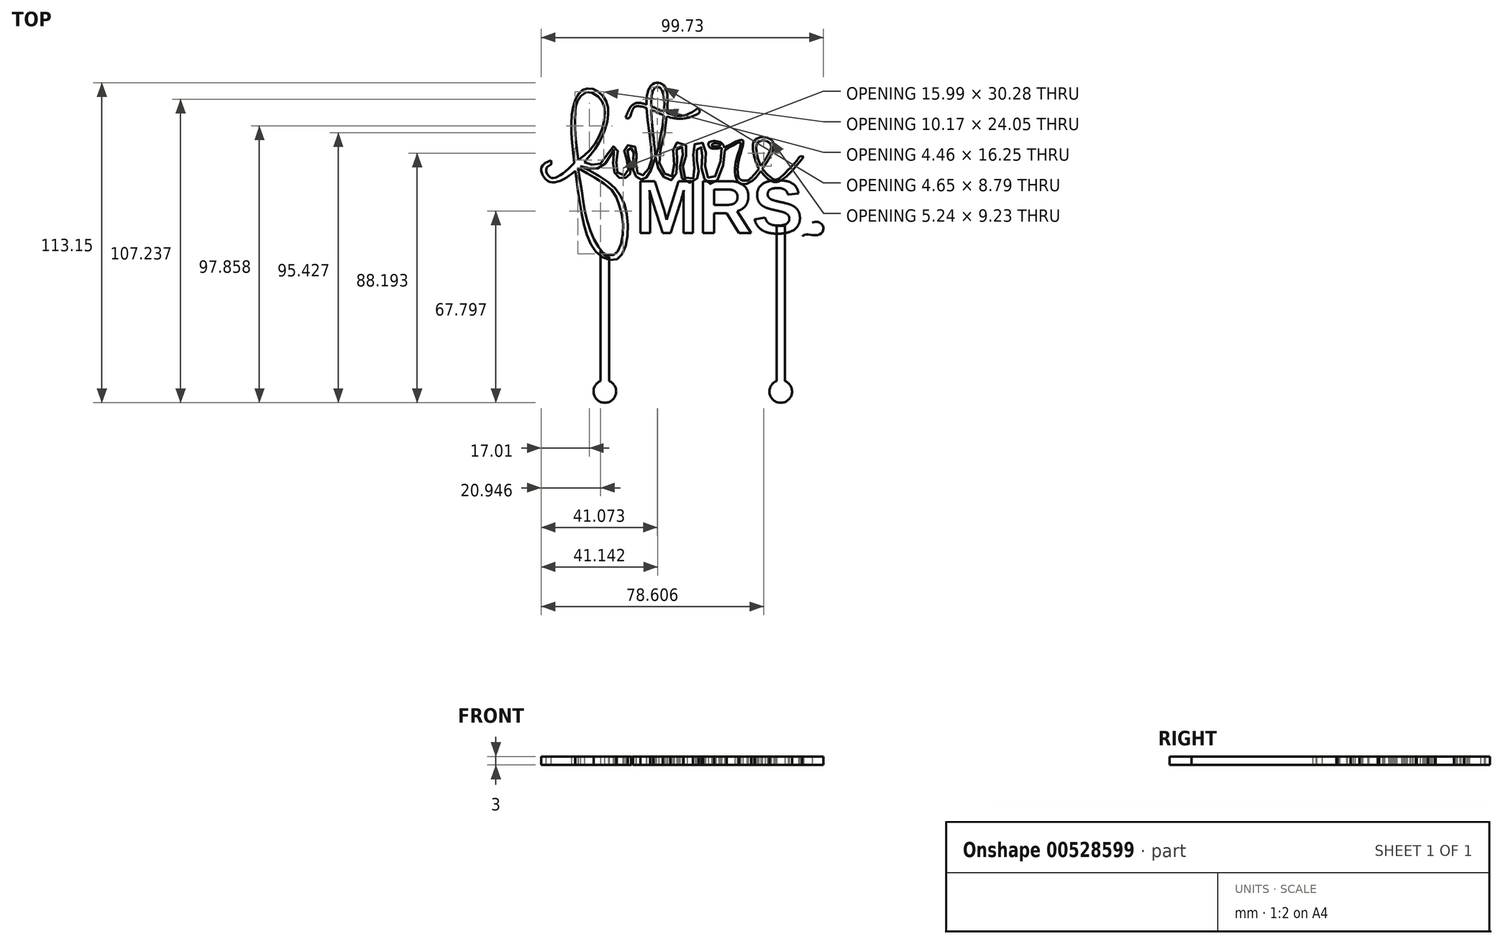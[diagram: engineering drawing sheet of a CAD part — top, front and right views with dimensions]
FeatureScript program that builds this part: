
annotation { "Feature Type Name" : "Feature", "Feature Type Description" : "" }
export const myFeature = defineFeature(function(context is Context, id is Id, definition is map)
    precondition{}
    {
        {
            var Q0;
            Q0=qCreatedBy(makeId("Top.planeOp"),FACE);
            var sketch = newSketch(context, id + "F0", { "sketchPlane" : qUnion([Q0])});
            skFitSpline(sketch, "E0", {"points": [v(-51.87, 23.02) * mm, v(-55.24, 20.26) * mm, v(-52.02, 15.35) * mm, v(-40.05, 22.4) * mm, v(-32.53, 34.53) * mm, v(-32.84, 44.96) * mm, v(-39.6, 48.34) * mm, v(-44.2, 40.97) * mm, v(-43.27, 19.8) * mm], "startDerivative": vector(-56.95, -24.54) * mm, "endDerivative": vector(16.5, -127.47) * mm});
            skFitSpline(sketch, "E1", {"points": [v(-43.27, 19.8) * mm, v(-40.66, 2.76) * mm, v(-35.45, -9.82) * mm, v(-28.08, -11.66) * mm, v(-24.7, 0) * mm, v(-28.85, 12.74) * mm, v(-41.42, 21.01) * mm], "startDerivative": vector(11.66, -89.63) * mm, "endDerivative": vector(-80.17, 39.6) * mm});
            skFitSpline(sketch, "E2", {"points": [v(-41.42, 21.01) * mm, v(-33.59, 21.01) * mm, v(-29.62, 26.7) * mm, v(-29.77, 19.8) * mm, v(-26.24, 16.57) * mm, v(-23.48, 19.8) * mm, v(-24.7, 26.85) * mm, v(-23.02, 27) * mm, v(-22.86, 19.8) * mm, v(-20.1, 16.27) * mm, v(-16.42, 19.8) * mm, v(-12.12, 46.34) * mm, v(-14.42, 48.95) * mm, v(-16.11, 46.65) * mm, v(-15.04, 25.93) * mm], "startDerivative": vector(109.8, -35.16) * mm, "endDerivative": vector(23.98, -203.73) * mm});
            skFitSpline(sketch, "E3", {"points": [v(-15.04, 25.93) * mm, v(-13.66, 19.49) * mm, v(-9.67, 15.96) * mm, v(-7.21, 20.1) * mm, v(-7.06, 27.45) * mm, v(-5.22, 27.45) * mm, v(-6.3, 20.1) * mm, v(-3.68, 15.2) * mm, v(0, 17.03) * mm, v(0, 21.02) * mm, v(0, 27.45) * mm, v(1.38, 27.45) * mm, v(1.38, 20.4) * mm, v(3.53, 15.2) * mm, v(6.17, 15.2) * mm, v(9.51, 27.45) * mm, v(6.44, 29.77) * mm, v(3.84, 29.16) * mm, v(4.45, 27.45) * mm, v(8.44, 27.45) * mm], "startDerivative": vector(7.62, -103.74) * mm, "endDerivative": vector(95.94, 18.45) * mm});
            skFitSpline(sketch, "E4", {"points": [v(9.51, 27.45) * mm, v(15.96, 30.08) * mm, v(14.27, 21.8) * mm, v(15.8, 15.2) * mm, v(23.17, 22.25) * mm, v(25.67, 30.33) * mm, v(20.56, 30.54) * mm, v(19.64, 25.93) * mm, v(21.33, 20.4) * mm], "startDerivative": vector(68.66, 40.43) * mm, "endDerivative": vector(17.69, -46.52) * mm});
            skFitSpline(sketch, "E5", {"points": [v(21.33, 20.4) * mm, v(27.47, 15.35) * mm, v(37.44, 24.25) * mm], "startDerivative": vector(13.32, -17.6) * mm, "endDerivative": vector(18.68, 23.5) * mm});
            skFitSpline(sketch, "E6", {"points": [v(-25.47, 38.06) * mm, v(-21.48, 43.27) * mm, v(-7.52, 38.82) * mm, v(0, 41.43) * mm], "startDerivative": vector(9.54, 26.43) * mm, "endDerivative": vector(21.11, 15.03) * mm});
            skFitSpline(sketch, "E7", {"points": [v(-51.87, 23.02) * mm, v(-51.87, 21.48) * mm, v(-53.42, 20.4) * mm, v(-51.87, 16.88) * mm, v(-43.27, 22.35) * mm], "startDerivative": vector(2.87, -11.23) * mm, "endDerivative": vector(24.01, 23.19) * mm});
            skFitSpline(sketch, "E8", {"points": [v(-43.27, 22.35) * mm, v(-37.68, 27.11) * mm, v(-33.7, 34.47) * mm, v(-32.93, 41.51) * mm, v(-34.77, 45.2) * mm, v(-39.14, 47.18) * mm, v(-42.5, 43.74) * mm, v(-43.27, 40.06) * mm, v(-43.27, 32.93) * mm, v(-42.66, 27.19) * mm, v(-42.2, 23.36) * mm], "startDerivative": vector(51.64, 37.29) * mm, "endDerivative": vector(5.1, -44.4) * mm});
            skFitSpline(sketch, "E9", {"points": [v(-42.2, 19.8) * mm, v(-40.74, 10.64) * mm, v(-39.44, 3.05) * mm, v(-36.76, -4.6) * mm, v(-34.3, -8.67) * mm, v(-32.43, -10.35) * mm, v(-29.54, -10.35) * mm, v(-27.35, -7.47) * mm, v(-26.36, 0) * mm, v(-27.75, 7.18) * mm, v(-30.24, 12.35) * mm, v(-36.91, 17.23) * mm, v(-41.42, 19.8) * mm], "startDerivative": vector(14.83, -89.85) * mm, "endDerivative": vector(-52.66, 29.4) * mm});
            skFitSpline(sketch, "E10", {"points": [v(-42.2, 23.36) * mm, v(-42.16, 23.16) * mm], "startDerivative": vector(0.04, -0.2) * mm, "endDerivative": vector(0.04, -0.2) * mm});
            skFitSpline(sketch, "E11", {"points": [v(-42.2, 19.8) * mm, v(-42.34, 20.13) * mm], "startDerivative": vector(-0.14, 0.34) * mm, "endDerivative": vector(-0.14, 0.34) * mm});
            skFitSpline(sketch, "E12", {"points": [v(-41.42, 19.8) * mm, v(-42.2, 20.27) * mm], "startDerivative": vector(-0.78, 0.47) * mm, "endDerivative": vector(-0.78, 0.47) * mm});
            skFitSpline(sketch, "E13", {"points": [v(-40.05, 22.4) * mm, v(-37.22, 21.43) * mm, v(-33.59, 22.4) * mm, v(-30.35, 27.72) * mm, v(-28.48, 27.33) * mm, v(-28.78, 22.4) * mm, v(-27.9, 18.19) * mm, v(-25.24, 18) * mm, v(-24.45, 21.01) * mm, v(-25.83, 25.46) * mm, v(-25.53, 27.92) * mm, v(-22.88, 28.3) * mm, v(-21.7, 26.54) * mm, v(-21.8, 22.4) * mm, v(-21.21, 18.48) * mm, v(-19.74, 17.6) * mm, v(-17.48, 19.76) * mm, v(-16.2, 23.79) * mm, v(-17.08, 32.63) * mm, v(-17.97, 40.1) * mm, v(-17.77, 46.68) * mm, v(-15.51, 50.22) * mm, v(-12.66, 50.02) * mm, v(-10.9, 47.07) * mm, v(-11.1, 37.15) * mm, v(-12.37, 29.78) * mm, v(-13.65, 23.79) * mm, v(-12.47, 19.49) * mm, v(-10.4, 17.4) * mm, v(-9.03, 17.4) * mm, v(-8.24, 21.01) * mm, v(-8.73, 26.74) * mm, v(-7.95, 29) * mm, v(-5.59, 29.39) * mm, v(-3.72, 27.52) * mm, v(-4.21, 24.28) * mm, v(-5.3, 21.01) * mm, v(-4.8, 17.4) * mm, v(-2.84, 16.03) * mm, v(-0.97, 17.6) * mm, v(-1.37, 21.01) * mm, v(-1.56, 26.25) * mm, v(-1.07, 28.7) * mm, v(0.8, 29.49) * mm, v(2.56, 28.4) * mm, v(2.76, 24.28) * mm, v(2.76, 19.49) * mm, v(4.04, 16.52) * mm, v(5.61, 16.62) * mm, v(8.07, 22.4) * mm, v(8.44, 27.45) * mm], "startDerivative": vector(148.32, -66.8) * mm, "endDerivative": vector(-1.3, 199.27) * mm});
            skFitSpline(sketch, "E14", {"points": [v(-25.47, 38.06) * mm, v(-24.16, 38.06) * mm, v(-22.88, 41.18) * mm, v(-21.01, 42.16) * mm, v(-16.44, 40.88) * mm, v(-11.99, 38.93) * mm, v(-6.55, 37.68) * mm, v(-1.27, 38.82) * mm, v(0.8, 40.3) * mm, v(0, 41.43) * mm], "startDerivative": vector(20.75, -6.65) * mm, "endDerivative": vector(-18.17, 17) * mm});
            skFitSpline(sketch, "E15", {"points": [v(7.9, 28.55) * mm, v(6.44, 29.16) * mm, v(4.48, 29.06) * mm, v(4.54, 28.07) * mm, v(6.17, 27.8) * mm, v(7.84, 27.93) * mm, v(7.9, 28.55) * mm]});
            skFitSpline(sketch, "E16", {"points": [v(9.64, 26.68) * mm, v(12.75, 28.52) * mm, v(15.01, 29.34) * mm, v(15.2, 28.49) * mm, v(13.91, 24.24) * mm, v(13.27, 21.22) * mm, v(13.49, 17) * mm, v(14.92, 14.8) * mm, v(17.3, 14.69) * mm], "startDerivative": vector(21.33, 13.15) * mm, "endDerivative": vector(22.5, 2.7) * mm});
            skFitSpline(sketch, "E17", {"points": [v(17.3, 14.69) * mm, v(19.93, 16.32) * mm, v(22.26, 19.2) * mm], "startDerivative": vector(5.74, 2.93) * mm, "endDerivative": vector(4.2, 6.05) * mm});
            skFitSpline(sketch, "E18", {"points": [v(25.67, 30.33) * mm, v(26.92, 28.58) * mm, v(24.17, 22) * mm, v(22.26, 19.2) * mm], "startDerivative": vector(4.75, 0) * mm, "endDerivative": vector(-5.33, -7.18) * mm});
            skFitSpline(sketch, "E19", {"points": [v(22.8, 19.94) * mm, v(25.67, 17.14) * mm, v(27.74, 16.18) * mm, v(31.58, 19.2) * mm, v(35.28, 23.24) * mm, v(36.17, 24.4) * mm, v(37.44, 24.25) * mm], "startDerivative": vector(14.06, -16.05) * mm, "endDerivative": vector(13.13, -4.08) * mm});
            skPoint(sketch, "E20.1.internal.orphan", {"position": v(21.62, 30.33) * mm});
            skPoint(sketch, "E20.4.internal.orphan", {"position": v(22.26, 20.9) * mm});
            skFitSpline(sketch, "E21", {"points": [v(22.26, 20.9) * mm, v(20.75, 26.26) * mm, v(21.62, 30.33) * mm, v(24.24, 30.33) * mm, v(26.1, 28.38) * mm], "startDerivative": vector(-6.12, 16.7) * mm, "endDerivative": vector(7, -8.44) * mm});
            skLineSegment(sketch, "E22", {"start": v(22.26, 20.9) * mm, "end": v(22.8, 19.94) * mm});
            skPoint(sketch, "E23", {"position": v(-14.88, 24.08) * mm});
            skFitSpline(sketch, "E24", {"points": [v(-14.95, 24.8) * mm, v(-14.85, 24.63) * mm, v(-14.67, 24.8) * mm], "startDerivative": vector(0.18, -0.53) * mm, "endDerivative": vector(0.34, 0.54) * mm});
            skFitSpline(sketch, "E25", {"points": [v(14.4, 17) * mm, v(15.47, 16) * mm, v(17.86, 15.95) * mm], "startDerivative": vector(2.06, -2.76) * mm, "endDerivative": vector(4.77, 0.53) * mm});
            skFitSpline(sketch, "E26", {"points": [v(5.27, 27.81) * mm, v(5.02, 28.55) * mm, v(6.17, 29.16) * mm, v(6.44, 29.16) * mm], "startDerivative": vector(-1.48, 2.37) * mm, "endDerivative": vector(1.06, -0.21) * mm});
            skFitSpline(sketch, "E27", {"points": [v(25.6, 28.99) * mm, v(25.93, 27.61) * mm, v(25.2, 25.72) * mm], "startDerivative": vector(1.28, -2.98) * mm, "endDerivative": vector(-1.83, -3.79) * mm});
            skFitSpline(sketch, "E28", {"points": [v(25.6, 28.99) * mm, v(23.97, 29.98) * mm, v(22.55, 30.05) * mm, v(20.87, 28.99) * mm], "startDerivative": vector(-4.87, 3.37) * mm, "endDerivative": vector(-4.82, -3.77) * mm});
            skFitSpline(sketch, "E29", {"points": [v(26.92, 28.58) * mm, v(26.26, 29.99) * mm, v(24.68, 30.96) * mm], "startDerivative": vector(-0.97, 3.22) * mm, "endDerivative": vector(-3.48, 1.56) * mm});
            skFitSpline(sketch, "E30", {"points": [v(5.81, 29.05) * mm, v(7.46, 28.88) * mm], "startDerivative": vector(1.67, 0.36) * mm, "endDerivative": vector(1.9, -0.4) * mm});
            skFitSpline(sketch, "E31", {"points": [v(5.1, 28.09) * mm, v(6.17, 27.8) * mm, v(7.84, 28.09) * mm], "startDerivative": vector(2.22, -0.91) * mm, "endDerivative": vector(3.19, 0.85) * mm});
            skFitSpline(sketch, "E32", {"points": [v(7.84, 28.09) * mm, v(7.98, 28.3) * mm, v(7.95, 28.44) * mm], "startDerivative": vector(0.34, 0.39) * mm, "endDerivative": vector(-0.14, 0.31) * mm});
            skFitSpline(sketch, "E33", {"points": [v(5.1, 28.09) * mm, v(5.02, 28.25) * mm], "startDerivative": vector(-0.08, 0.17) * mm, "endDerivative": vector(-0.08, 0.17) * mm});
            skFitSpline(sketch, "E34", {"points": [v(5.02, 28.55) * mm, v(4.99, 28.45) * mm, v(5.1, 28.09) * mm, v(5.77, 27.97) * mm, v(6.5, 27.95) * mm, v(7.25, 27.93) * mm, v(7.9, 28.16) * mm, v(7.9, 28.55) * mm], "startDerivative": vector(-0.66, -1.2) * mm, "endDerivative": vector(-0.92, 3.39) * mm});
            skSolve(sketch);
        }
        {
            var Q0;
            Q0=qCreatedBy(makeId("Top.planeOp"),FACE);
            var sketch = newSketch(context, id + "F1", { "sketchPlane" : qUnion([Q0])});
            skText(sketch, "E35", { "text": "MRS", "fontName": "Arimo-Bold.ttf"});
            const initialGuessF1  = {"E35": [-0.02206, -0.00264, 1, 0, 0.01918]};
            skSetInitialGuess(sketch, initialGuessF1);
            skSolve(sketch);
        }
        {
            var Q0;
            Q0=qCreatedBy(makeId("Top.planeOp"),FACE);
            var sketch = newSketch(context, id + "F2", { "sketchPlane" : qUnion([Q0])});
            skFitSpline(sketch, "E36", {"points": [v(40.46, 0.96) * mm, v(40.38, 2.47) * mm, v(39.6, 3.64) * mm, v(38.12, 4.3) * mm, v(36.3, 3.53) * mm, v(35.89, 0.85) * mm, v(37.03, -2.2) * mm, v(36.85, -3.83) * mm], "startDerivative": vector(0.7, 12.55) * mm, "endDerivative": vector(-3.44, -11.68) * mm});
            skFitSpline(sketch, "E37.MirrorCS", {"points": [v(40.46, 0.96) * mm, v(41.93, 1.3) * mm, v(43.27, 0.87) * mm, v(44.32, -0.37) * mm, v(44.07, -2.34) * mm, v(41.61, -3.47) * mm, v(38.36, -3.21) * mm, v(36.85, -3.83) * mm], "startDerivative": vector(11.88, 4.12) * mm, "endDerivative": vector(-10.29, -6.52) * mm});
            skSolve(sketch);
        }
        {
            var Q0;
            Q0=qCreatedBy(makeId("Top.planeOp"),FACE);
            var sketch = newSketch(context, id + "F3", { "sketchPlane" : qUnion([Q0])});
            skLineSegment(sketch, "E38.top", {"start": v(-5, -44.18) * mm, "end": v(-1.92, -44.18) * mm});
            skLineSegment(sketch, "E39.top", {"start": v(-34.3, -58.67) * mm, "end": v(-31.3, -58.67) * mm});
            skLineSegment(sketch, "E39.left", {"start": v(-34.3, -8.67) * mm, "end": v(-34.3, -58.67) * mm});
            skLineSegment(sketch, "E39.right", {"start": v(-31.3, -10.6) * mm, "end": v(-31.3, -58.67) * mm});
            skLineSegment(sketch, "E40.bottom", {"start": v(27.83, -0.18) * mm, "end": v(30.83, -0.18) * mm});
            skLineSegment(sketch, "E40.top", {"start": v(27.83, -58.67) * mm, "end": v(30.83, -58.67) * mm});
            skLineSegment(sketch, "E40.left", {"start": v(27.83, -0.18) * mm, "end": v(27.83, -58.67) * mm});
            skLineSegment(sketch, "E40.right", {"start": v(30.83, -0.18) * mm, "end": v(30.83, -58.67) * mm});
            skPoint(sketch, "E41", {"position": v(-31.3, -10.6) * mm});
            skLineSegment(sketch, "E42", {"start": v(-31.3, -58.67) * mm, "end": v(27.83, -58.67) * mm, "construction": true});
            skCircle(sketch, "E43", {"center": v(-32.8, -58.67) * mm, "radius": 4 * mm});
            skCircle(sketch, "E44", {"center": v(29.33, -58.67) * mm, "radius": 4 * mm});
            skFitSpline(sketch, "E45.0", {"points": [v(-42.2, 19.8) * mm, v(-41.68, 16.65) * mm, v(-40.7, 10.65) * mm, v(-39.76, 3.16) * mm, v(-37.07, -4.55) * mm, v(-34.46, -8.6) * mm, v(-32.66, -10.66) * mm, v(-29.15, -10.82) * mm, v(-26.89, -7.39) * mm, v(-25.84, 0.13) * mm, v(-27.68, 7.17) * mm, v(-29.54, 12.82) * mm, v(-36.93, 17.29) * mm, v(-40.04, 19.03) * mm, v(-41.42, 19.8) * mm]});
            skSolve(sketch);
        }
        {
            var Q0;
            {var subQ0=sQuery(id+"F0.wireOp",EDGE,"E7");var subQ1=sQuery(id+"F0.wireOp",EDGE,"E0");var subQ2=makeQuery(id+"F0.imprint","INTERSECT",VERTEX,{"disambiguationData":[OD(0.0)],"derivedFrom":[subQ1,subQ0]});Q0=makeQuery(id+"F0.imprint","IMPRINT",FACE,{"disambiguationData":[TD([[makeQuery(id+"F0.imprint","IMPRINT",EDGE,{"disambiguationData":[TD([[subQ2,-1.0]])],"derivedFrom":subQ1}),1.0]])]});}
            var Q1;
            Q1=makeQuery(id+"F0.imprint","IMPRINT",FACE,{"disambiguationData":[TD([[makeQuery(id+"F0.imprint","IMPRINT",EDGE,{"derivedFrom":sQuery(id+"F0.wireOp",EDGE,"E9")}),-1.0]])]});
            var Q2;
            {var subQ6=sQuery(id+"F0.wireOp",EDGE,"E10");Q2=makeQuery(id+"F0.imprint","IMPRINT",FACE,{"disambiguationData":[TD([[makeQuery(id+"F0.imprint","IMPRINT",EDGE,{"derivedFrom":subQ6}),-1.0]])]});}
            var Q3;
            {var subQ0=sQuery(id+"F0.wireOp",EDGE,"E3");var subQ1=sQuery(id+"F0.wireOp",EDGE,"E2");var subQ2=makeQuery(id+"F0.imprint","INTERSECT",VERTEX,{"disambiguationData":[OD(0.0)],"derivedFrom":[subQ1,subQ0]});Q3=makeQuery(id+"F0.imprint","IMPRINT",FACE,{"disambiguationData":[TD([[makeQuery(id+"F0.imprint","IMPRINT",EDGE,{"disambiguationData":[TD([[subQ2,1.0]])],"derivedFrom":subQ1}),-1.0]])]});}
            var Q4;
            {var subQ0=sQuery(id+"F0.wireOp",EDGE,"E14");var subQ1=sQuery(id+"F0.wireOp",EDGE,"E6");var subQ2=makeQuery(id+"F0.imprint","INTERSECT",VERTEX,{"disambiguationData":[OD(0.0)],"derivedFrom":[subQ1,subQ0]});Q4=makeQuery(id+"F0.imprint","IMPRINT",FACE,{"disambiguationData":[TD([[makeQuery(id+"F0.imprint","IMPRINT",EDGE,{"disambiguationData":[TD([[subQ2,-1.0]])],"derivedFrom":subQ1}),-1.0]])]});}
            var Q5;
            {var subQ0=sQuery(id+"F0.wireOp",EDGE,"E6");var subQ1=sQuery(id+"F0.wireOp",EDGE,"E2");var subQ2=makeQuery(id+"F0.imprint","INTERSECT",VERTEX,{"disambiguationData":[OD(0.0)],"derivedFrom":[subQ1,subQ0]});Q5=makeQuery(id+"F0.imprint","IMPRINT",FACE,{"disambiguationData":[TD([[makeQuery(id+"F0.imprint","IMPRINT",EDGE,{"disambiguationData":[TD([[subQ2,-1.0]])],"derivedFrom":subQ1}),-1.0]])]});}
            var Q6;
            {var subQ0=sQuery(id+"F0.wireOp",EDGE,"E14");var subQ1=sQuery(id+"F0.wireOp",EDGE,"E2");var subQ2=makeQuery(id+"F0.imprint","INTERSECT",VERTEX,{"disambiguationData":[OD(0.0)],"derivedFrom":[subQ1,subQ0]});Q6=makeQuery(id+"F0.imprint","IMPRINT",FACE,{"disambiguationData":[TD([[makeQuery(id+"F0.imprint","IMPRINT",EDGE,{"disambiguationData":[TD([[subQ2,-1.0]])],"derivedFrom":subQ1}),1.0]])]});}
            var Q7;
            {var subQ0=sQuery(id+"F0.wireOp",EDGE,"E14");var subQ1=sQuery(id+"F0.wireOp",EDGE,"E6");var subQ2=makeQuery(id+"F0.imprint","INTERSECT",VERTEX,{"disambiguationData":[OD(1.0)],"derivedFrom":[subQ1,subQ0]});Q7=makeQuery(id+"F0.imprint","IMPRINT",FACE,{"disambiguationData":[TD([[makeQuery(id+"F0.imprint","IMPRINT",EDGE,{"disambiguationData":[TD([[subQ2,1.0]])],"derivedFrom":subQ1}),-1.0]])]});}
            var Q8;
            Q8=makeQuery(id+"F0.imprint","IMPRINT",FACE,{"disambiguationData":[TD([[makeQuery(id+"F0.imprint","IMPRINT",EDGE,{"derivedFrom":sQuery(id+"F0.wireOp",EDGE,"E15")}),-1.0]])]});
            var Q9;
            {var subQ0=sQuery(id+"F0.wireOp",EDGE,"E14");var subQ1=sQuery(id+"F0.wireOp",EDGE,"E2");var subQ2=makeQuery(id+"F0.imprint","INTERSECT",VERTEX,{"disambiguationData":[OD(0.0)],"derivedFrom":[subQ1,subQ0]});Q9=makeQuery(id+"F0.imprint","IMPRINT",FACE,{"disambiguationData":[TD([[makeQuery(id+"F0.imprint","IMPRINT",EDGE,{"disambiguationData":[TD([[subQ2,-1.0]])],"derivedFrom":subQ1}),-1.0]])]});}
            var Q10;
            {var subQ0=sQuery(id+"F0.wireOp",EDGE,"E6");var subQ1=sQuery(id+"F0.wireOp",EDGE,"E2");var subQ2=makeQuery(id+"F0.imprint","INTERSECT",VERTEX,{"disambiguationData":[OD(1.0)],"derivedFrom":[subQ1,subQ0]});Q10=makeQuery(id+"F0.imprint","IMPRINT",FACE,{"disambiguationData":[TD([[makeQuery(id+"F0.imprint","IMPRINT",EDGE,{"disambiguationData":[TD([[subQ2,-1.0]])],"derivedFrom":subQ1}),-1.0]])]});}
            var Q11;
            {var subQ4=sQuery(id+"F0.wireOp",EDGE,"E16");Q11=makeQuery(id+"F0.imprint","IMPRINT",FACE,{"disambiguationData":[TD([[makeQuery(id+"F0.imprint","IMPRINT",EDGE,{"derivedFrom":subQ4}),1.0]])]});}
            var Q12;
            {var subQ5=sQuery(id+"F0.wireOp",EDGE,"E21");Q12=makeQuery(id+"F0.imprint","IMPRINT",FACE,{"disambiguationData":[TD([[makeQuery(id+"F0.imprint","IMPRINT",EDGE,{"derivedFrom":subQ5}),1.0]])]});}
            var Q13;
            {var subQ1=sQuery(id+"F0.wireOp",EDGE,"E4");var subQ3=sQuery(id+"F0.wireOp",EDGE,"E5");var subQ4=makeQuery(id+"F0.imprint","INTERSECT",VERTEX,{"disambiguationData":[OD(1.0)],"derivedFrom":[subQ1,subQ3]});Q13=makeQuery(id+"F0.imprint","IMPRINT",FACE,{"disambiguationData":[TD([[makeQuery(id+"F0.imprint","IMPRINT",EDGE,{"disambiguationData":[TD([[subQ4,-1.0]])],"derivedFrom":subQ1}),-1.0]])]});}
            var Q14;
            {var subQ2=sQuery(id+"F0.wireOp",EDGE,"E4");var subQ5=sQuery(id+"F0.wireOp",EDGE,"E18");var subQ6=makeQuery(id+"F0.imprint","INTERSECT",VERTEX,{"derivedFrom":[subQ2,subQ5]});Q14=makeQuery(id+"F0.imprint","IMPRINT",FACE,{"disambiguationData":[TD([[makeQuery(id+"F0.imprint","IMPRINT",EDGE,{"disambiguationData":[TD([[subQ6,1.0]])],"derivedFrom":subQ2}),-1.0]])]});}
            var Q15;
            {var subQ0=sQuery(id+"F0.wireOp",EDGE,"E19");Q15=makeQuery(id+"F0.imprint","IMPRINT",FACE,{"disambiguationData":[TD([[makeQuery(id+"F0.imprint","IMPRINT",EDGE,{"derivedFrom":subQ0}),-1.0]])]});}
            var Q16;
            {var subQ0=sQuery(id+"F0.wireOp",EDGE,"E3");var subQ1=sQuery(id+"F0.wireOp",EDGE,"E2");var subQ2=makeQuery(id+"F0.imprint","INTERSECT",VERTEX,{"disambiguationData":[OD(1.0)],"derivedFrom":[subQ1,subQ0]});Q16=makeQuery(id+"F0.imprint","IMPRINT",FACE,{"disambiguationData":[TD([[makeQuery(id+"F0.imprint","IMPRINT",EDGE,{"disambiguationData":[TD([[subQ2,-1.0]])],"derivedFrom":subQ1}),1.0]])]});}
            var Q17;
            Q17 = qSketchRegion(id + "F1", true);
            var Q18;
            Q18=makeQuery(id+"F2.imprint","IMPRINT",FACE,{"disambiguationData":[TD([[makeQuery(id+"F2.imprint","IMPRINT",EDGE,{"derivedFrom":sQuery(id+"F2.wireOp",EDGE,"E36")}),1.0]])]});
            var Q19;
            {var subQ0=sQuery(id+"F3.wireOp",EDGE,"E39.top");Q19=makeQuery(id+"F3.imprint","IMPRINT",FACE,{"disambiguationData":[TD([[makeQuery(id+"F3.imprint","IMPRINT",EDGE,{"derivedFrom":subQ0}),-1.0]])]});}
            var Q20;
            {var subQ0=sQuery(id+"F3.wireOp",EDGE,"E40.top");Q20=makeQuery(id+"F3.imprint","IMPRINT",FACE,{"disambiguationData":[TD([[makeQuery(id+"F3.imprint","IMPRINT",EDGE,{"derivedFrom":subQ0}),-1.0]])]});}
            var Q21;
            {var subQ0=sQuery(id+"F3.wireOp",EDGE,"E40.bottom");Q21=makeQuery(id+"F3.imprint","IMPRINT",FACE,{"disambiguationData":[TD([[makeQuery(id+"F3.imprint","IMPRINT",EDGE,{"derivedFrom":subQ0}),-1.0]])]});}
            var Q22;
            {var subQ0=sQuery(id+"F3.wireOp",EDGE,"E40.top");Q22=makeQuery(id+"F3.imprint","IMPRINT",FACE,{"disambiguationData":[TD([[makeQuery(id+"F3.imprint","IMPRINT",EDGE,{"derivedFrom":subQ0}),1.0]])]});}
            var Q23;
            {var subQ0=sQuery(id+"F3.wireOp",EDGE,"E45.0");var subQ1=sQuery(id+"F3.wireOp",EDGE,"E39.left");var subQ2=makeQuery(id+"F3.imprint","INTERSECT",VERTEX,{"derivedFrom":[subQ1,subQ0]});Q23=makeQuery(id+"F3.imprint","IMPRINT",FACE,{"disambiguationData":[TD([[makeQuery(id+"F3.imprint","IMPRINT",EDGE,{"disambiguationData":[TD([[subQ2,-1.0]])],"derivedFrom":subQ1}),1.0]])]});}
            var Q24;
            {var subQ0=sQuery(id+"F3.wireOp",EDGE,"E39.top");Q24=makeQuery(id+"F3.imprint","IMPRINT",FACE,{"disambiguationData":[TD([[makeQuery(id+"F3.imprint","IMPRINT",EDGE,{"derivedFrom":subQ0}),1.0]])]});}
            var Q25;
            {var subQ5=sQuery(id+"F0.wireOp",EDGE,"E28");Q25=makeQuery(id+"F0.imprint","IMPRINT",FACE,{"disambiguationData":[TD([[makeQuery(id+"F0.imprint","IMPRINT",EDGE,{"derivedFrom":subQ5}),-1.0]])]});}
            var Q26;
            {var subQ0=sQuery(id+"F0.wireOp",EDGE,"E18");var subQ1=sQuery(id+"F0.wireOp",EDGE,"E4");var subQ2=makeQuery(id+"F0.imprint","INTERSECT",VERTEX,{"derivedFrom":[subQ1,subQ0]});Q26=makeQuery(id+"F0.imprint","IMPRINT",FACE,{"disambiguationData":[TD([[makeQuery(id+"F0.imprint","IMPRINT",EDGE,{"disambiguationData":[TD([[subQ2,-1.0]])],"derivedFrom":subQ1}),-1.0]])]});}
            var Q27;
            {var subQ0=sQuery(id+"F0.wireOp",EDGE,"E25");Q27=makeQuery(id+"F0.imprint","IMPRINT",FACE,{"disambiguationData":[TD([[makeQuery(id+"F0.imprint","IMPRINT",EDGE,{"derivedFrom":subQ0}),-1.0]])]});}
            var Q28;
            {var subQ0=sQuery(id+"F0.wireOp",EDGE,"E26");Q28=makeQuery(id+"F0.imprint","IMPRINT",FACE,{"disambiguationData":[TD([[makeQuery(id+"F0.imprint","IMPRINT",EDGE,{"derivedFrom":subQ0}),1.0]])]});}
            var Q29;
            {var subQ0=sQuery(id+"F0.wireOp",EDGE,"E31");var subQ1=sQuery(id+"F0.wireOp",EDGE,"E15");var subQ2=makeQuery(id+"F0.imprint","INTERSECT",VERTEX,{"disambiguationData":[OD(1.0)],"derivedFrom":[subQ1,subQ0]});Q29=makeQuery(id+"F0.imprint","IMPRINT",FACE,{"disambiguationData":[TD([[makeQuery(id+"F0.imprint","IMPRINT",EDGE,{"disambiguationData":[TD([[subQ2,-1.0]])],"derivedFrom":subQ1}),1.0]])]});}
            var Q30;
            {var subQ0=sQuery(id+"F0.wireOp",EDGE,"E30");Q30=makeQuery(id+"F0.imprint","IMPRINT",FACE,{"disambiguationData":[TD([[makeQuery(id+"F0.imprint","IMPRINT",EDGE,{"derivedFrom":subQ0}),1.0]])]});}
            var Q31;
            {var subQ5=sQuery(id+"F0.wireOp",EDGE,"E33");Q31=makeQuery(id+"F0.imprint","IMPRINT",FACE,{"disambiguationData":[TD([[makeQuery(id+"F0.imprint","IMPRINT",EDGE,{"derivedFrom":subQ5}),1.0]])]});}
            var Q32;
            {var subQ3=sQuery(id+"F0.wireOp",EDGE,"E26");var subQ5=sQuery(id+"F0.wireOp",EDGE,"E15");var subQ8=makeQuery(id+"F0.imprint","INTERSECT",VERTEX,{"disambiguationData":[OD(0.0)],"derivedFrom":[subQ5,subQ3]});Q32=makeQuery(id+"F0.imprint","IMPRINT",FACE,{"disambiguationData":[TD([[makeQuery(id+"F0.imprint","IMPRINT",EDGE,{"disambiguationData":[TD([[subQ8,-1.0]])],"derivedFrom":subQ5}),1.0]])]});}
            var Q33;
            {var subQ0=sQuery(id+"F0.wireOp",EDGE,"E31");var subQ1=sQuery(id+"F0.wireOp",EDGE,"E15");var subQ2=makeQuery(id+"F0.imprint","INTERSECT",VERTEX,{"disambiguationData":[OD(0.0)],"derivedFrom":[subQ1,subQ0]});Q33=makeQuery(id+"F0.imprint","IMPRINT",FACE,{"disambiguationData":[TD([[makeQuery(id+"F0.imprint","IMPRINT",EDGE,{"disambiguationData":[TD([[subQ2,-1.0]])],"derivedFrom":subQ1}),1.0]])]});}
            extrude(context, id + "F4", {"entities" : qUnion([Q0, Q1, Q2, Q3, Q4, Q5, Q6, Q7, Q8, Q9, Q10, Q11, Q12, Q13, Q14, Q15, Q16, Q17, Q18, Q19, Q20, Q21, Q22, Q23, Q24, Q25, Q26, Q27, Q28, Q29, Q30, Q31, Q32, Q33]), "depth" : 3 * mm, "offsetDistance" : 25.4 * mm});
        }
    });
